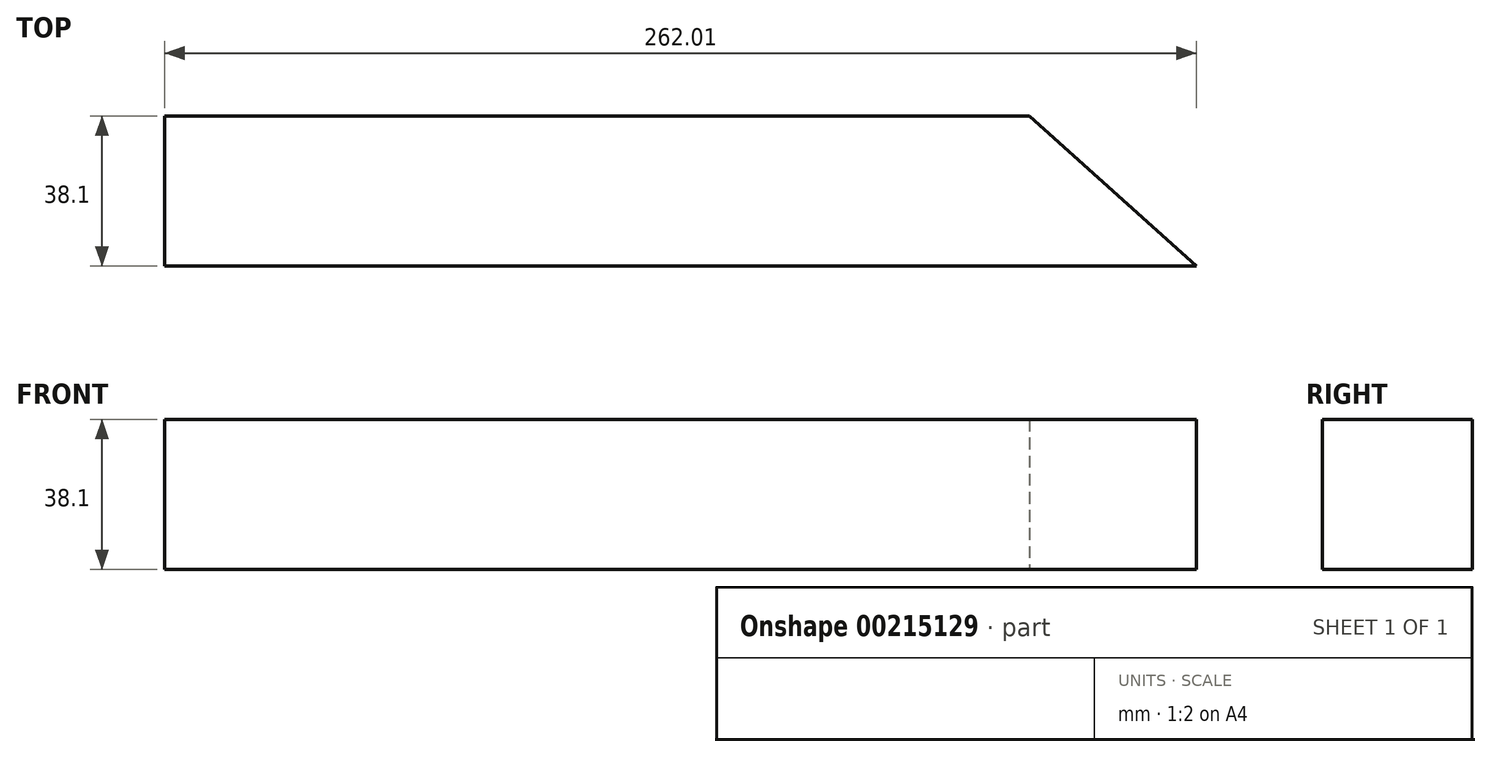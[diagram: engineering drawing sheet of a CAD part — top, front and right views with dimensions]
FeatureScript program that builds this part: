
annotation { "Feature Type Name" : "Feature", "Feature Type Description" : "" }
export const myFeature = defineFeature(function(context is Context, id is Id, definition is map)
    precondition{}
    {
        {
            var Q0;
            Q0=qCreatedBy(makeId("Top.planeOp"),FACE);
            var sketch = newSketch(context, id + "F0", { "sketchPlane" : qUnion([Q0])});
            skLineSegment(sketch, "E0", {"start": v(0, 0) * mm, "end": v(262, 0) * mm});
            skLineSegment(sketch, "E1", {"start": v(262, 0) * mm, "end": v(219.7, 38.1) * mm});
            skLineSegment(sketch, "E2", {"start": v(219.7, 38.1) * mm, "end": v(0, 38.1) * mm});
            skLineSegment(sketch, "E3", {"start": v(0, 38.1) * mm, "end": v(0, 0) * mm});
            skSolve(sketch);
        }
        {
            var Q0;
            Q0=makeQuery(id+"F0.imprint","IMPRINT",FACE,{"disambiguationData":[TD([[makeQuery(id+"F0.imprint","IMPRINT",EDGE,{"derivedFrom":sQuery(id+"F0.wireOp",EDGE,"E0")}),1.0]])]});
            extrude(context, id + "F1", {"entities" : qUnion([Q0]), "depth" : 38.1 * mm, "offsetDistance" : 25.4 * mm});
        }
    });
